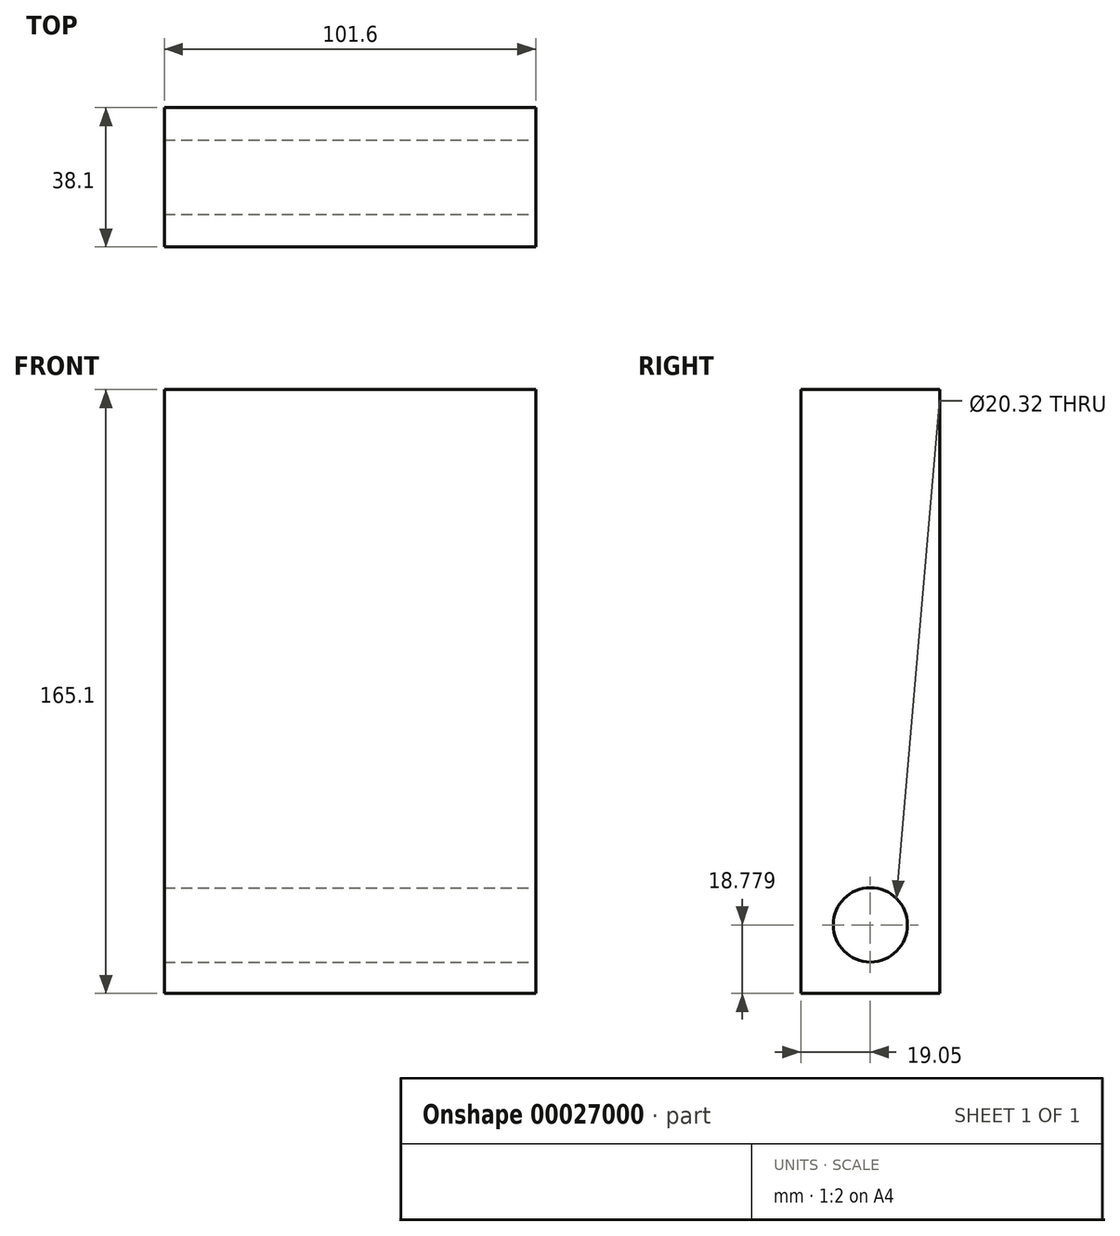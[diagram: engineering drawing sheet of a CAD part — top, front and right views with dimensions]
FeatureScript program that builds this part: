
annotation { "Feature Type Name" : "Feature", "Feature Type Description" : "" }
export const myFeature = defineFeature(function(context is Context, id is Id, definition is map)
    precondition{}
    {
        {
            var Q0;
            Q0=qCreatedBy(makeId("Front.planeOp"),FACE);
            var sketch = newSketch(context, id + "F0", { "sketchPlane" : qUnion([Q0])});
            skLineSegment(sketch, "E0", {"start": v(0, 0) * mm, "end": v(101.6, 0) * mm});
            skLineSegment(sketch, "E1", {"start": v(101.6, 0) * mm, "end": v(101.6, 165.1) * mm});
            skLineSegment(sketch, "E2", {"start": v(101.6, 165.1) * mm, "end": v(0, 165.1) * mm});
            skLineSegment(sketch, "E3", {"start": v(0, 165.1) * mm, "end": v(0, 0) * mm});
            skSolve(sketch);
        }
        {
            var Q0;
            Q0=makeQuery(id+"F0.imprint","IMPRINT",FACE,{"disambiguationData":[TD([[makeQuery(id+"F0.imprint","IMPRINT",EDGE,{"derivedFrom":sQuery(id+"F0.wireOp",EDGE,"E0")}),1.0]])]});
            extrude(context, id + "F1", {"entities" : qUnion([Q0]), "depth" : 38.1 * mm});
        }
        {
            var Q0;
            Q0=makeQuery(id+"F1.opExtrude","SWEPT_FACE",FACE,{"disambiguationData":[OSD([sQuery(id+"F0.wireOp",EDGE,"E1")])]});
            var sketch = newSketch(context, id + "F2", { "sketchPlane" : qUnion([Q0])});
            skLineSegment(sketch, "E4", {"start": v(-19.05, 0) * mm, "end": v(-19.05, 18.78) * mm});
            skCircle(sketch, "E5", {"center": v(-19.05, 18.78) * mm, "radius": 10.16 * mm});
            skSolve(sketch);
        }
        {
            var Q0;
            Q0=makeQuery(id+"F2.imprint","IMPRINT",FACE,{"disambiguationData":[TD([[makeQuery(id+"F2.imprint","IMPRINT",EDGE,{"derivedFrom":sQuery(id+"F2.wireOp",EDGE,"E5")}),1.0]])]});
            extrude(context, id + "F3", {"entities" : qUnion([Q0]), "operationType" : NewBodyOperationType.REMOVE, "endBound" : BoundingType.THROUGH_ALL, "oppositeDirection" : true, "depth" : 25.4 * mm});
        }
    });
